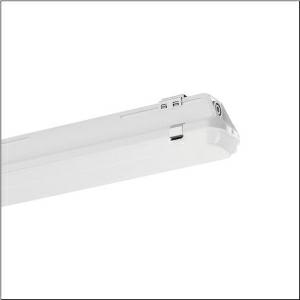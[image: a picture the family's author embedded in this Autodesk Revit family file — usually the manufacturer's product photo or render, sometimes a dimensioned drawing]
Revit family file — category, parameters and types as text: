
# Revit family: monsun_21_51fb10dl420k
name_source: partatom
category: Lighting Fixtures
units: mm (PartAtom-declared; Revit-internal decimal feet)

## family parameters
Cut with Voids When Loaded = No
Host = Face
Light Source = No
Part Type = Normal
Room Calculation Point = No
Round Connector Dimension = Use Diameter
Shared = No

## types (1)
- --- (1 x LED, 2630 lm, 15.4 W, 4000K)
    Apparent Load = 15 VA
    CIE Flux Codes = 46 76 93 94 100
    Color Rendering = 80
    Color Temperature = 4000K
    Default Elevation = 1800 mm
    Description = Monsun 21, damp-proof luminaire, chain hanger, primary optical cover: enclosure, of PMMA, light emission: direct distribution, primary light characteristic: symmetric, installation type: suspended mounting, surface-mounted, horizontal mounting, vertical mounting, LED, rated luminous flux: 2.630lm, luminous efficacy: 171lm/W, light colour: 840, colour temperature: 4000K, control gear: DALI 2, with terminal, 5-pole, max. 2.5mm², mains connection: 220..240V, AC, 50/60Hz, rated input power: 15W, housing, of glass-fibre reinforced plastic, uncoated, bright grey, incl. chain hanger, length: 1.299mm, width: 90mm, height: 88mm, clip for enclosure, of stainless steel (V2A), ceiling mounting element, of stainless steel (V2A), chain hanger, of stainless steel (V2A), protection rating (complete): IP66, insulation class (complete): insulation class I (protective earthing), certification: CE, ENEC, VDE, UKCA, protection symbol: D, impact resistance: IK04, permissible operating ambient temperature: -25..+35°C, standard: EN 50419, EN 60598-2-1, corresponds to IFS (International Featured Standards) requirements for safety and quality in the food industry, for indoor or canopied outdoor use, no direct snow, no direct sun, no direct rain, LABS conformity tested according to VDMA 24364:2018-05, contact your sales advisor before using the luminaires in applications with unclear chemical exposure, large temperature fluctuations or condensation-forming humidity, packaging unit: 1 piece
    Height = 88 mm
    Lamp = 1 x LED
    Lamp Light Flux = 2630 lm
    Lamp Power = 15.4 W
    Lamp count = 1
    Length = 1299 mm
    Luminous efficacy = 171 lm/W
    Manufacturer = Siteco
    ModVariant = No
    Model = 51FB10DL420K
    Mounting Place = Ceiling
    Mounting Type = Surface mounted
    Number of Poles = 1
    OnlyDefault = Yes
    Power Factor = 1
    Product Name = Monsun 21
    Product group = damp-proof luminaire
    ProductGroupID = 300
    Protection Class = Protection class I
    Protection Degree = IP 66
    RLX_Detail_Level = 1
    RLX_Emergency_Light_Flux = 0 lm
    RLX_Emergency_Type = 0
    RLX_Emergency_Type_DB = No
    RlxData = <blob elided: 92981 chars, md5=25c25107>
    Socket = socket
    Standby Power = 0 W
    System Light Flux = 2630 lm
    System Power = 15 W
    Type Comments = factory setting: luminous flux: 100 % | dim-lin: 254 | 98 mA
    Type Image = l_1319656.jpg
    URL = http://relux.com
    VarID = @adj_037349
    Voltage = 0 V
    Weight = 0.00 kg
    Width = 90 mm

## geometry (parser evidence)
native form markers: Blend x4, Sweep x15
no freeform markers — native parametric forms only
